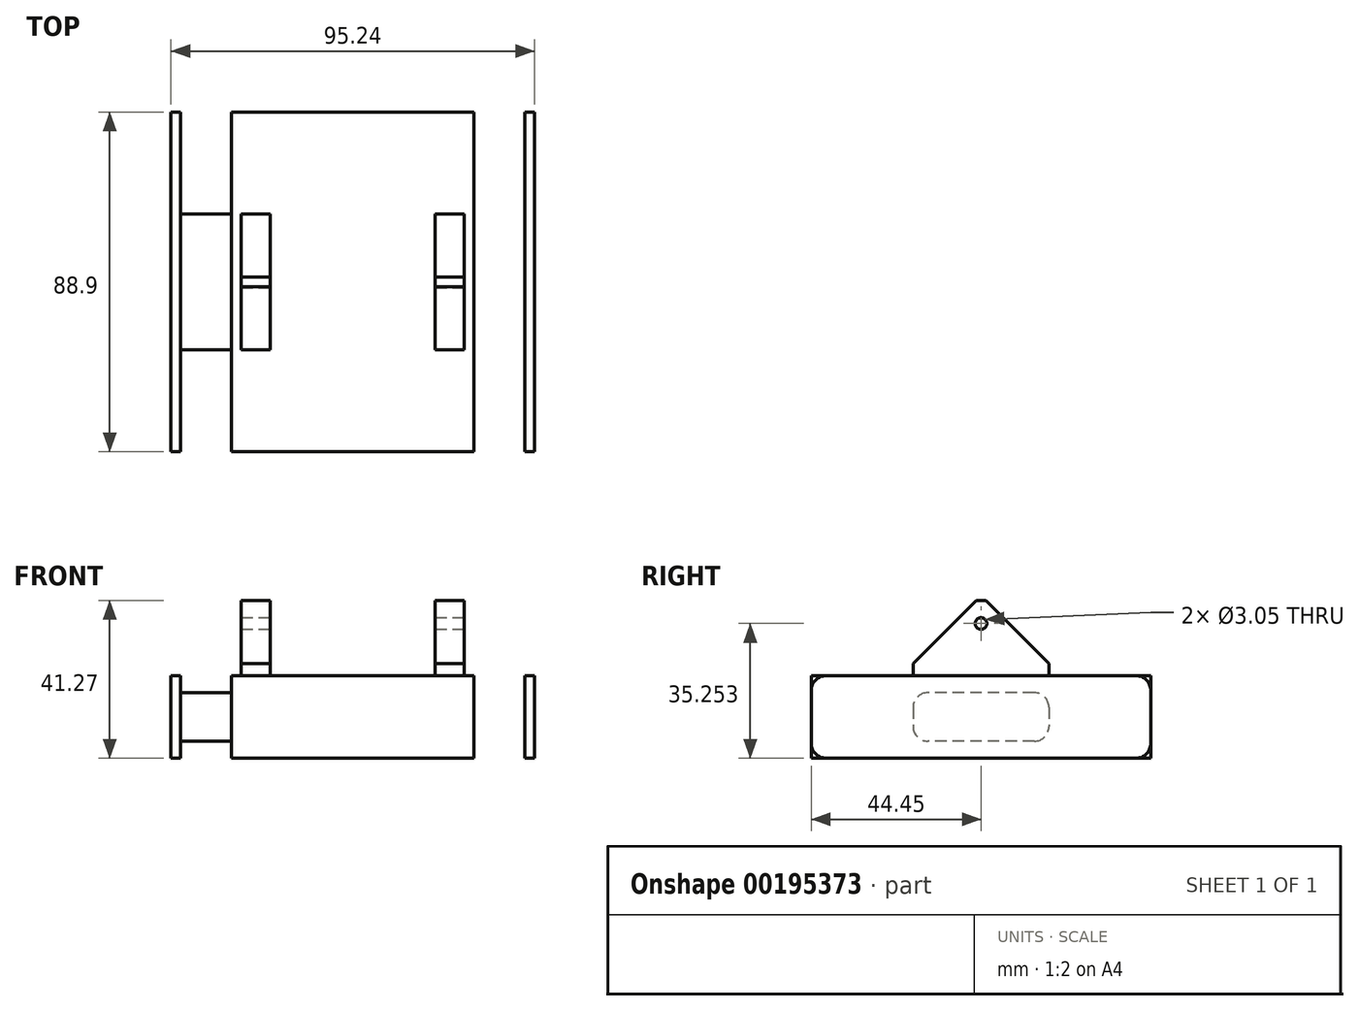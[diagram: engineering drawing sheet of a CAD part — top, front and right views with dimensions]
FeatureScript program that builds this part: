
annotation { "Feature Type Name" : "Feature", "Feature Type Description" : "" }
export const myFeature = defineFeature(function(context is Context, id is Id, definition is map)
    precondition{}
    {
        {
            var Q0;
            Q0=qCreatedBy(makeId("Top.planeOp"),FACE);
            var sketch = newSketch(context, id + "F0", { "sketchPlane" : qUnion([Q0])});
            skLineSegment(sketch, "E0.bottom", {"start": v(-31.75, 44.45) * mm, "end": v(31.75, 44.45) * mm});
            skLineSegment(sketch, "E0.top", {"start": v(-31.75, -44.45) * mm, "end": v(31.75, -44.45) * mm});
            skLineSegment(sketch, "E0.left", {"start": v(-45.09, 44.45) * mm, "end": v(-45.09, -44.45) * mm});
            skLineSegment(sketch, "E0.right", {"start": v(45.09, 44.45) * mm, "end": v(45.09, -44.45) * mm});
            skPoint(sketch, "E0.middle", {"position": v(0, 0) * mm});
            skLineSegment(sketch, "E1.left", {"start": v(-31.75, 44.45) * mm, "end": v(-31.75, -44.45) * mm});
            skLineSegment(sketch, "E1.right", {"start": v(31.75, 44.45) * mm, "end": v(31.75, -44.45) * mm});
            skLineSegment(sketch, "E2.bottom", {"start": v(-47.63, 44.45) * mm, "end": v(-45.09, 44.45) * mm});
            skLineSegment(sketch, "E2.left", {"start": v(-47.62, 44.45) * mm, "end": v(-47.62, -44.45) * mm});
            skLineSegment(sketch, "E2.right", {"start": v(47.62, 44.45) * mm, "end": v(47.62, -44.45) * mm});
            skLineSegment(sketch, "E3.bottom", {"start": v(-45.09, 17.78) * mm, "end": v(-31.75, 17.78) * mm});
            skLineSegment(sketch, "E3.top", {"start": v(-45.09, -17.78) * mm, "end": v(-31.75, -17.78) * mm});
            skLineSegment(sketch, "E3.left", {"start": v(-45.09, 17.78) * mm, "end": v(-45.09, -17.78) * mm});
            skLineSegment(sketch, "E3.right", {"start": v(45.09, 17.78) * mm, "end": v(45.09, -17.78) * mm});
            skLineSegment(sketch, "E4.trimOffspring", {"start": v(31.75, 17.78) * mm, "end": v(45.09, 17.78) * mm});
            skLineSegment(sketch, "E5.trimOffspring", {"start": v(31.75, -17.78) * mm, "end": v(45.09, -17.78) * mm});
            skLineSegment(sketch, "E6.bottom", {"start": v(-31.75, -44.45) * mm, "end": v(-29.21, -44.45) * mm});
            skLineSegment(sketch, "E7.right", {"start": v(31.75, -31.72) * mm, "end": v(31.75, -44.45) * mm});
            skLineSegment(sketch, "E8.trimOffspring", {"start": v(45.09, 44.45) * mm, "end": v(47.63, 44.45) * mm});
            skLineSegment(sketch, "E9.right", {"start": v(47.62, -31.75) * mm, "end": v(47.62, -44.45) * mm});
            skLineSegment(sketch, "E10.right", {"start": v(-47.63, -31.75) * mm, "end": v(-47.63, -44.45) * mm});
            skLineSegment(sketch, "E11.bottom", {"start": v(-29.21, 17.78) * mm, "end": v(-21.59, 17.78) * mm});
            skLineSegment(sketch, "E11.top", {"start": v(-29.21, -17.78) * mm, "end": v(-21.59, -17.78) * mm});
            skLineSegment(sketch, "E11.left", {"start": v(-29.21, 17.78) * mm, "end": v(-29.21, -17.78) * mm});
            skLineSegment(sketch, "E11.right", {"start": v(-21.59, 17.78) * mm, "end": v(-21.59, -17.78) * mm});
            skLineSegment(sketch, "E12.bottom", {"start": v(29.21, 17.78) * mm, "end": v(21.59, 17.78) * mm});
            skLineSegment(sketch, "E12.top", {"start": v(29.21, -17.78) * mm, "end": v(21.59, -17.78) * mm});
            skLineSegment(sketch, "E12.left", {"start": v(29.21, 17.78) * mm, "end": v(29.21, -17.78) * mm});
            skLineSegment(sketch, "E12.right", {"start": v(21.59, 17.78) * mm, "end": v(21.59, -17.78) * mm});
            skLineSegment(sketch, "E13", {"start": v(-47.62, -44.45) * mm, "end": v(-45.09, -44.45) * mm});
            skPoint(sketch, "E14.orphan", {"position": v(-47.63, -47) * mm});
            skPoint(sketch, "E15.orphan", {"position": v(31.75, -47) * mm});
            skPoint(sketch, "E16.orphan", {"position": v(47.62, -47) * mm});
            skLineSegment(sketch, "E17", {"start": v(45.09, -44.45) * mm, "end": v(47.62, -44.45) * mm});
            skSolve(sketch);
        }
        {
            var Q0;
            {var subQ11=sQuery(id+"F0.wireOp",EDGE,"E0.bottom");Q0=makeQuery(id+"F0.imprint","IMPRINT",FACE,{"disambiguationData":[TD([[makeQuery(id+"F0.imprint","IMPRINT",EDGE,{"derivedFrom":subQ11}),-1.0]])]});}
            var Q1;
            {var subQ0=sQuery(id+"F0.wireOp",EDGE,"E2.bottom");Q1=makeQuery(id+"F0.imprint","IMPRINT",FACE,{"disambiguationData":[TD([[makeQuery(id+"F0.imprint","IMPRINT",EDGE,{"derivedFrom":subQ0}),-1.0]])]});}
            var Q2;
            Q2=makeQuery(id+"F0.imprint","IMPRINT",FACE,{"disambiguationData":[TD([[makeQuery(id+"F0.imprint","IMPRINT",EDGE,{"derivedFrom":sQuery(id+"F0.wireOp",EDGE,"E2.right")}),-1.0]])]});
            extrude(context, id + "F1", {"entities" : qUnion([Q0, Q1, Q2]), "endBound" : BoundingType.SYMMETRIC, "depth" : 21.59 * mm});
        }
        {
            var Q0;
            {var subQ0=sQuery(id+"F0.wireOp",EDGE,"E3.bottom");Q0=makeQuery(id+"F0.imprint","IMPRINT",FACE,{"disambiguationData":[TD([[makeQuery(id+"F0.imprint","IMPRINT",EDGE,{"derivedFrom":subQ0}),-1.0]])]});}
            var Q1;
            Q1=makeQuery(id+"F0.imprint","IMPRINT",FACE,{"disambiguationData":[TD([[makeQuery(id+"F0.imprint","IMPRINT",EDGE,{"derivedFrom":sQuery(id+"F0.wireOp",EDGE,"E3.right")}),-1.0]])]});
            extrude(context, id + "F2", {"entities" : qUnion([Q0, Q1]), "endBound" : BoundingType.SYMMETRIC, "depth" : 12.7 * mm});
        }
        {
            var Q0;
            Q0=makeQuery(id+"F0.imprint","IMPRINT",FACE,{"disambiguationData":[TD([[makeQuery(id+"F0.imprint","IMPRINT",EDGE,{"derivedFrom":sQuery(id+"F0.wireOp",EDGE,"E12.bottom")}),1.0]])]});
            var Q1;
            Q1=makeQuery(id+"F0.imprint","IMPRINT",FACE,{"disambiguationData":[TD([[makeQuery(id+"F0.imprint","IMPRINT",EDGE,{"derivedFrom":sQuery(id+"F0.wireOp",EDGE,"E11.bottom")}),-1.0]])]});
            extrude(context, id + "F3", {"entities" : qUnion([Q0, Q1]), "operationType" : NewBodyOperationType.ADD, "oppositeDirection" : true, "depth" : 10.8 * mm});
        }
        {
            var Q0;
            Q0=makeQuery(id+"F0.imprint","IMPRINT",FACE,{"disambiguationData":[TD([[makeQuery(id+"F0.imprint","IMPRINT",EDGE,{"derivedFrom":sQuery(id+"F0.wireOp",EDGE,"E12.bottom")}),1.0]])]});
            var Q1;
            Q1=makeQuery(id+"F0.imprint","IMPRINT",FACE,{"disambiguationData":[TD([[makeQuery(id+"F0.imprint","IMPRINT",EDGE,{"derivedFrom":sQuery(id+"F0.wireOp",EDGE,"E11.bottom")}),-1.0]])]});
            extrude(context, id + "F4", {"entities" : qUnion([Q0, Q1]), "operationType" : NewBodyOperationType.ADD, "depth" : 30.48 * mm});
        }
        {
            var Q0;
            Q0=makeQuery(id+"F2.opExtrude","CAP_EDGE",EDGE,{"disambiguationData":[OSD([sQuery(id+"F0.wireOp",EDGE,"E5.trimOffspring")])],"isStart":false});
            var Q1;
            Q1=makeQuery(id+"F2.opExtrude","CAP_EDGE",EDGE,{"disambiguationData":[OSD([sQuery(id+"F0.wireOp",EDGE,"E5.trimOffspring")])],"isStart":true});
            var Q2;
            Q2=makeQuery(id+"F2.opExtrude","CAP_EDGE",EDGE,{"disambiguationData":[OSD([sQuery(id+"F0.wireOp",EDGE,"E4.trimOffspring")])],"isStart":false});
            var Q3;
            Q3=makeQuery(id+"F2.opExtrude","CAP_EDGE",EDGE,{"disambiguationData":[OSD([sQuery(id+"F0.wireOp",EDGE,"E4.trimOffspring")])],"isStart":true});
            var Q4;
            Q4=makeQuery(id+"F2.opExtrude","CAP_EDGE",EDGE,{"disambiguationData":[OSD([sQuery(id+"F0.wireOp",EDGE,"E3.bottom")])],"isStart":true});
            var Q5;
            Q5=makeQuery(id+"F2.opExtrude","CAP_EDGE",EDGE,{"disambiguationData":[OSD([sQuery(id+"F0.wireOp",EDGE,"E3.top")])],"isStart":true});
            var Q6;
            Q6=makeQuery(id+"F2.opExtrude","CAP_EDGE",EDGE,{"disambiguationData":[OSD([sQuery(id+"F0.wireOp",EDGE,"E3.bottom")])],"isStart":false});
            var Q7;
            Q7=makeQuery(id+"F2.opExtrude","CAP_EDGE",EDGE,{"disambiguationData":[OSD([sQuery(id+"F0.wireOp",EDGE,"E3.top")])],"isStart":false});
            fillet(context, id + "F5", {"entities" : qUnion([Q0, Q1, Q2, Q3, Q4, Q5, Q6, Q7]), "radius" : 3.8 * mm, "tangentPropagation" : true, "allowEdgeOverflow" : false});
        }
        {
            var Q0;
            Q0=makeQuery(id+"F4.opExtrude","CAP_EDGE",EDGE,{"disambiguationData":[OSD([sQuery(id+"F0.wireOp",EDGE,"E12.bottom")])],"isStart":false});
            var Q1;
            Q1=makeQuery(id+"F4.opExtrude","CAP_EDGE",EDGE,{"disambiguationData":[OSD([sQuery(id+"F0.wireOp",EDGE,"E11.bottom")])],"isStart":false});
            var Q2;
            Q2=makeQuery(id+"F4.opExtrude","CAP_EDGE",EDGE,{"disambiguationData":[OSD([sQuery(id+"F0.wireOp",EDGE,"E12.top")])],"isStart":false});
            var Q3;
            Q3=makeQuery(id+"F4.opExtrude","CAP_EDGE",EDGE,{"disambiguationData":[OSD([sQuery(id+"F0.wireOp",EDGE,"E11.top")])],"isStart":false});
            chamfer(context, id + "F6", {"entities" : qUnion([Q0, Q1, Q2, Q3]), "width" : 16.5 * mm, "tangentPropagation" : true});
        }
        {
            var Q0;
            Q0=makeQuery(id+"F4.opExtrude","SWEPT_FACE",FACE,{"disambiguationData":[OSD([sQuery(id+"F0.wireOp",EDGE,"E12.left")])]});
            var sketch = newSketch(context, id + "F7", { "sketchPlane" : qUnion([Q0])});
            skCircle(sketch, "E18", {"center": v(0, 24.46) * mm, "radius": 1.52 * mm});
            skPoint(sketch, "E18.centerSnap0", {"position": v(0, 30.48) * mm});
            skSolve(sketch);
        }
        {
            var Q0;
            Q0=makeQuery(id+"F7.imprint","IMPRINT",FACE,{"disambiguationData":[TD([[makeQuery(id+"F7.imprint","IMPRINT",EDGE,{"derivedFrom":sQuery(id+"F7.wireOp",EDGE,"E18")}),1.0]])]});
            extrude(context, id + "F8", {"entities" : qUnion([Q0]), "operationType" : NewBodyOperationType.REMOVE, "endBound" : BoundingType.THROUGH_ALL, "oppositeDirection" : true, "depth" : 25.4 * mm});
        }
        {
            var Q0;
            Q0=makeQuery(id+"F1.opExtrude","CAP_EDGE",EDGE,{"disambiguationData":[OSD([sQuery(id+"F0.wireOp",EDGE,"E9.top")])],"isStart":false});
            var Q1;
            Q1=makeQuery(id+"F1.opExtrude","CAP_EDGE",EDGE,{"disambiguationData":[OSD([sQuery(id+"F0.wireOp",EDGE,"E8.trimOffspring")])],"isStart":false});
            var Q2;
            Q2=makeQuery(id+"F1.opExtrude","CAP_EDGE",EDGE,{"disambiguationData":[OSD([sQuery(id+"F0.wireOp",EDGE,"E10.top")])],"isStart":false});
            var Q3;
            Q3=makeQuery(id+"F1.opExtrude","CAP_EDGE",EDGE,{"disambiguationData":[OSD([sQuery(id+"F0.wireOp",EDGE,"E10.top")])],"isStart":true});
            var Q4;
            Q4=makeQuery(id+"F1.opExtrude","CAP_EDGE",EDGE,{"disambiguationData":[OSD([sQuery(id+"F0.wireOp",EDGE,"E9.top")])],"isStart":true});
            var Q5;
            Q5=makeQuery(id+"F1.opExtrude","CAP_EDGE",EDGE,{"disambiguationData":[OSD([sQuery(id+"F0.wireOp",EDGE,"E2.bottom")])],"isStart":false});
            var Q6;
            Q6=makeQuery(id+"F1.opExtrude","CAP_EDGE",EDGE,{"disambiguationData":[OSD([sQuery(id+"F0.wireOp",EDGE,"E2.bottom")])],"isStart":true});
            var Q7;
            Q7=makeQuery(id+"F1.opExtrude","CAP_EDGE",EDGE,{"disambiguationData":[OSD([sQuery(id+"F0.wireOp",EDGE,"E8.trimOffspring")])],"isStart":true});
            var Q8;
            Q8=makeQuery(id+"F1.opExtrude","CAP_EDGE",EDGE,{"disambiguationData":[OSD([sQuery(id+"F0.wireOp",EDGE,"E13")])],"isStart":false});
            var Q9;
            Q9=makeQuery(id+"F1.opExtrude","CAP_EDGE",EDGE,{"disambiguationData":[OSD([sQuery(id+"F0.wireOp",EDGE,"E13")])],"isStart":true});
            var Q10;
            Q10=makeQuery(id+"F1.opExtrude","CAP_EDGE",EDGE,{"disambiguationData":[OSD([sQuery(id+"F0.wireOp",EDGE,"E17")])],"isStart":true});
            var Q11;
            Q11=makeQuery(id+"F1.opExtrude","CAP_EDGE",EDGE,{"disambiguationData":[OSD([sQuery(id+"F0.wireOp",EDGE,"E17")])],"isStart":false});
            fillet(context, id + "F9", {"entities" : qUnion([Q0, Q1, Q2, Q3, Q4, Q5, Q6, Q7, Q8, Q9, Q10, Q11]), "radius" : 3.8 * mm, "tangentPropagation" : true, "allowEdgeOverflow" : false});
        }
    });
